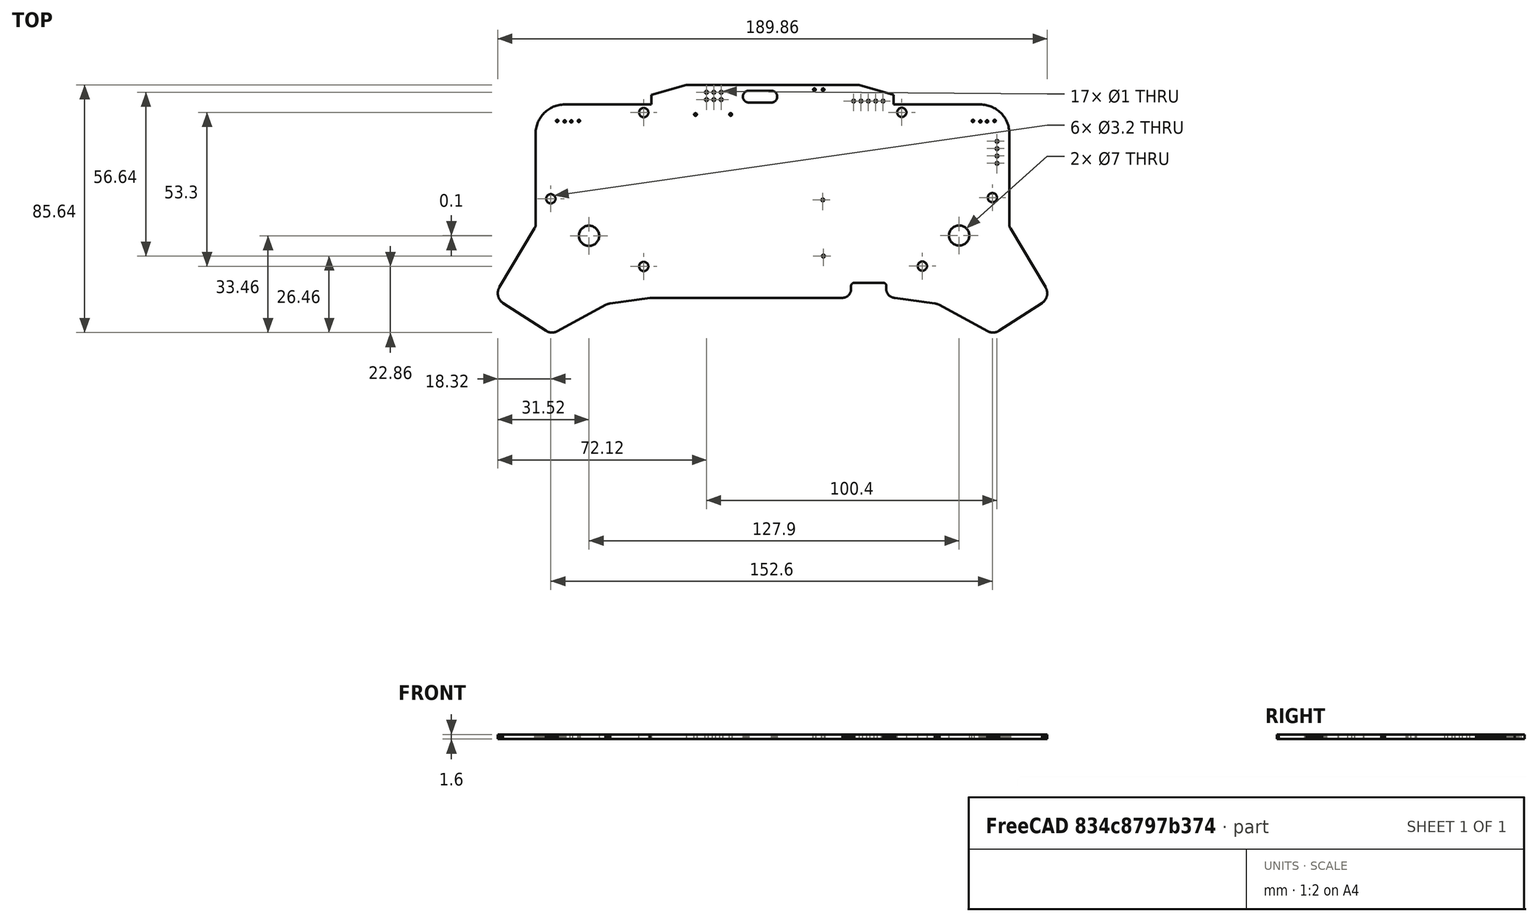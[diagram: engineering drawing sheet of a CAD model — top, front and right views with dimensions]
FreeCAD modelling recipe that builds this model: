
FCSTD DOCUMENT  (FreeCAD 0.21R33771 (Git))
Label: MilkFront
License: All rights reserved
LicenseURL: http://en.wikipedia.org/wiki/All_rights_reserved
objects: App::Part×4, Sketcher::SketchObject×2, PartDesign::CoordinateSystem×1, Part::Feature×1, PartDesign::ShapeBinder×1, PartDesign::Body×1
note: 6 computed .brp shape members not serialized (recipe doc carries the construction recipe); baked Part::Feature solids carry a one-line shape summary decoded from their .brp

FEATURE [PartDesign::CoordinateSystem] Local_CS_514c
  AttacherType = Attacher::AttachEngine3D
  MapMode = 2
  Support = -> [X_Axis003]
FEATURE [Part::Feature] Pcb_514c
  shape: bbox 189.9 x 85.64 x 1.6 mm, 543 faces (baked)
FEATURE [Sketcher::SketchObject] PCB_Sketch_514c
  FullyConstrained = false
  sketch-geometry (504):
    g0: LineSegment StartX=150.224 StartY=-25.4 StartZ=0 EndX=158 EndY=-25.4 EndZ=0
    g1: LineSegment StartX=158 StartY=-25.4 StartZ=0 EndX=158.106 EndY=-25.403 EndZ=0
    g2: LineSegment StartX=158.106 StartY=-25.403 StartZ=0 EndX=158.21 EndY=-25.4113 EndZ=0
    g3: LineSegment StartX=158.21 StartY=-25.4113 StartZ=0 EndX=158.312 EndY=-25.4246 EndZ=0
    g4: LineSegment StartX=158.312 StartY=-25.4246 StartZ=0 EndX=158.413 EndY=-25.443 EndZ=0
    g5: LineSegment StartX=158.413 StartY=-25.443 StartZ=0 EndX=158.513 EndY=-25.4662 EndZ=0
    g6: LineSegment StartX=158.513 StartY=-25.4662 StartZ=0 EndX=158.61 EndY=-25.4941 EndZ=0
    g7: LineSegment StartX=158.61 StartY=-25.4941 StartZ=0 EndX=158.705 EndY=-25.5266 EndZ=0
    g8: LineSegment StartX=158.705 StartY=-25.5266 StartZ=0 EndX=158.798 EndY=-25.5636 EndZ=0
    g9: LineSegment StartX=158.798 StartY=-25.5636 StartZ=0 EndX=158.889 EndY=-25.6049 EndZ=0
    g10: LineSegment StartX=158.889 StartY=-25.6049 StartZ=0 EndX=158.978 EndY=-25.6505 EndZ=0
    g11: LineSegment StartX=158.978 StartY=-25.6505 StartZ=0 EndX=159.063 EndY=-25.7001 EndZ=0
    g12: LineSegment StartX=159.063 StartY=-25.7001 StartZ=0 EndX=159.147 EndY=-25.7536 EndZ=0
    g13: LineSegment StartX=159.147 StartY=-25.7536 StartZ=0 EndX=159.227 EndY=-25.811 EndZ=0
    g14: LineSegment StartX=159.227 StartY=-25.811 StartZ=0 EndX=159.304 EndY=-25.8721 EndZ=0
    g15: LineSegment StartX=159.304 StartY=-25.8721 StartZ=0 EndX=159.379 EndY=-25.9367 EndZ=0
    g16: LineSegment StartX=159.379 StartY=-25.9367 StartZ=0 EndX=159.45 EndY=-26.0048 EndZ=0
    g17: LineSegment StartX=159.45 StartY=-26.0048 StartZ=0 EndX=159.518 EndY=-26.0762 EndZ=0
    g18: LineSegment StartX=159.518 StartY=-26.0762 StartZ=0 EndX=159.582 EndY=-26.1508 EndZ=0
    g19: LineSegment StartX=159.582 StartY=-26.1508 StartZ=0 EndX=159.643 EndY=-26.2284 EndZ=0
    g20: LineSegment StartX=159.643 StartY=-26.2284 StartZ=0 EndX=159.7 EndY=-26.3089 EndZ=0
    g21: LineSegment StartX=159.7 StartY=-26.3089 StartZ=0 EndX=159.753 EndY=-26.3923 EndZ=0
    g22: LineSegment StartX=159.753 StartY=-26.3923 StartZ=0 EndX=159.803 EndY=-26.4783 EndZ=0
    g23: LineSegment StartX=159.803 StartY=-26.4783 StartZ=0 EndX=159.848 EndY=-26.5668 EndZ=0
    g24: LineSegment StartX=159.848 StartY=-26.5668 StartZ=0 EndX=159.889 EndY=-26.6578 EndZ=0
    g25: LineSegment StartX=159.889 StartY=-26.6578 StartZ=0 EndX=159.926 EndY=-26.751 EndZ=0
    g26: LineSegment StartX=159.926 StartY=-26.751 StartZ=0 EndX=159.958 EndY=-26.8464 EndZ=0
    g27: LineSegment StartX=159.958 StartY=-26.8464 StartZ=0 EndX=159.985 EndY=-26.9438 EndZ=0
    g28: LineSegment StartX=159.985 StartY=-26.9438 StartZ=0 EndX=160.008 EndY=-27.0431 EndZ=0
    g29: LineSegment StartX=160.008 StartY=-27.0431 StartZ=0 EndX=160.026 EndY=-27.1442 EndZ=0
    g30: LineSegment StartX=160.026 StartY=-27.1442 StartZ=0 EndX=160.039 EndY=-27.2469 EndZ=0
    g31: LineSegment StartX=160.039 StartY=-27.2469 StartZ=0 EndX=160.047 EndY=-27.3511 EndZ=0
    g32: LineSegment StartX=160.047 StartY=-27.3511 StartZ=0 EndX=160.05 EndY=-27.4567 EndZ=0
    g33: LineSegment StartX=160.05 StartY=-27.4567 StartZ=0 EndX=160.047 EndY=-27.5623 EndZ=0
    g34: LineSegment StartX=160.047 StartY=-27.5623 StartZ=0 EndX=160.039 EndY=-27.6665 EndZ=0
    g35: LineSegment StartX=160.039 StartY=-27.6665 StartZ=0 EndX=160.026 EndY=-27.7692 EndZ=0
    g36: LineSegment StartX=160.026 StartY=-27.7692 StartZ=0 EndX=160.008 EndY=-27.8702 EndZ=0
    g37: LineSegment StartX=160.008 StartY=-27.8702 StartZ=0 EndX=159.985 EndY=-27.9695 EndZ=0
    g38: LineSegment StartX=159.985 StartY=-27.9695 StartZ=0 EndX=159.958 EndY=-28.0669 EndZ=0
    g39: LineSegment StartX=159.958 StartY=-28.0669 StartZ=0 EndX=159.926 EndY=-28.1623 EndZ=0
    g40: LineSegment StartX=159.926 StartY=-28.1623 StartZ=0 EndX=159.889 EndY=-28.2555 EndZ=0
    g41: LineSegment StartX=159.889 StartY=-28.2555 StartZ=0 EndX=159.848 EndY=-28.3465 EndZ=0
    g42: LineSegment StartX=159.848 StartY=-28.3465 StartZ=0 EndX=159.803 EndY=-28.435 EndZ=0
    g43: LineSegment StartX=159.803 StartY=-28.435 StartZ=0 EndX=159.753 EndY=-28.521 EndZ=0
    g44: LineSegment StartX=159.753 StartY=-28.521 StartZ=0 EndX=159.7 EndY=-28.6044 EndZ=0
    g45: LineSegment StartX=159.7 StartY=-28.6044 StartZ=0 EndX=159.643 EndY=-28.6849 EndZ=0
    g46: LineSegment StartX=159.643 StartY=-28.6849 StartZ=0 EndX=159.582 EndY=-28.7625 EndZ=0
    g47: LineSegment StartX=159.582 StartY=-28.7625 StartZ=0 EndX=159.518 EndY=-28.8371 EndZ=0
    g48: LineSegment StartX=159.518 StartY=-28.8371 StartZ=0 EndX=159.45 EndY=-28.9085 EndZ=0
    g49: LineSegment StartX=159.45 StartY=-28.9085 StartZ=0 EndX=159.379 EndY=-28.9766 EndZ=0
    g50: LineSegment StartX=159.379 StartY=-28.9766 StartZ=0 EndX=159.304 EndY=-29.0412 EndZ=0
    g51: LineSegment StartX=159.304 StartY=-29.0412 StartZ=0 EndX=159.227 EndY=-29.1023 EndZ=0
    g52: LineSegment StartX=159.227 StartY=-29.1023 StartZ=0 EndX=159.147 EndY=-29.1597 EndZ=0
    g53: LineSegment StartX=159.147 StartY=-29.1597 StartZ=0 EndX=159.063 EndY=-29.2133 EndZ=0
    g54: LineSegment StartX=159.063 StartY=-29.2133 StartZ=0 EndX=158.978 EndY=-29.2629 EndZ=0
    g55: LineSegment StartX=158.978 StartY=-29.2629 StartZ=0 EndX=158.889 EndY=-29.3084 EndZ=0
    g56: LineSegment StartX=158.889 StartY=-29.3084 StartZ=0 EndX=158.798 EndY=-29.3497 EndZ=0
    g57: LineSegment StartX=158.798 StartY=-29.3497 StartZ=0 EndX=158.705 EndY=-29.3867 EndZ=0
    g58: LineSegment StartX=158.705 StartY=-29.3867 StartZ=0 EndX=158.61 EndY=-29.4192 EndZ=0
    g59: LineSegment StartX=158.61 StartY=-29.4192 StartZ=0 EndX=158.513 EndY=-29.4471 EndZ=0
    g60: LineSegment StartX=158.513 StartY=-29.4471 StartZ=0 EndX=158.413 EndY=-29.4703 EndZ=0
    g61: LineSegment StartX=158.413 StartY=-29.4703 StartZ=0 EndX=158.312 EndY=-29.4887 EndZ=0
    g62: LineSegment StartX=158.312 StartY=-29.4887 StartZ=0 EndX=158.21 EndY=-29.5021 EndZ=0
    g63: LineSegment StartX=158.21 StartY=-29.5021 StartZ=0 EndX=158.106 EndY=-29.5103 EndZ=0
    g64: LineSegment StartX=158.106 StartY=-29.5103 StartZ=0 EndX=158 EndY=-29.5133 EndZ=0
    g65: LineSegment StartX=158 StartY=-29.5133 StartZ=0 EndX=150.224 EndY=-29.5133 EndZ=0
    g66: LineSegment StartX=150.224 StartY=-29.5133 StartZ=0 EndX=150.119 EndY=-29.5102 EndZ=0
    g67: LineSegment StartX=150.119 StartY=-29.5102 StartZ=0 EndX=150.014 EndY=-29.5019 EndZ=0
    g68: LineSegment StartX=150.014 StartY=-29.5019 StartZ=0 EndX=149.912 EndY=-29.4884 EndZ=0
    g69: LineSegment StartX=149.912 StartY=-29.4884 StartZ=0 EndX=149.811 EndY=-29.47 EndZ=0
    g70: LineSegment StartX=149.811 StartY=-29.47 StartZ=0 EndX=149.712 EndY=-29.4468 EndZ=0
    g71: LineSegment StartX=149.712 StartY=-29.4468 StartZ=0 EndX=149.614 EndY=-29.4188 EndZ=0
    g72: LineSegment StartX=149.614 StartY=-29.4188 StartZ=0 EndX=149.519 EndY=-29.3863 EndZ=0
    g73: LineSegment StartX=149.519 StartY=-29.3863 StartZ=0 EndX=149.426 EndY=-29.3493 EndZ=0
    g74: LineSegment StartX=149.426 StartY=-29.3493 StartZ=0 EndX=149.335 EndY=-29.3079 EndZ=0
    g75: LineSegment StartX=149.335 StartY=-29.3079 StartZ=0 EndX=149.247 EndY=-29.2623 EndZ=0
    g76: LineSegment StartX=149.247 StartY=-29.2623 StartZ=0 EndX=149.161 EndY=-29.2127 EndZ=0
    g77: LineSegment StartX=149.161 StartY=-29.2127 StartZ=0 EndX=149.078 EndY=-29.1591 EndZ=0
    g78: LineSegment StartX=149.078 StartY=-29.1591 StartZ=0 EndX=148.998 EndY=-29.1017 EndZ=0
    g79: LineSegment StartX=148.998 StartY=-29.1017 StartZ=0 EndX=148.921 EndY=-29.0407 EndZ=0
    g80: LineSegment StartX=148.921 StartY=-29.0407 StartZ=0 EndX=148.846 EndY=-28.976 EndZ=0
    g81: LineSegment StartX=148.846 StartY=-28.976 StartZ=0 EndX=148.775 EndY=-28.9079 EndZ=0
    g82: LineSegment StartX=148.775 StartY=-28.9079 StartZ=0 EndX=148.707 EndY=-28.8366 EndZ=0
    g83: LineSegment StartX=148.707 StartY=-28.8366 StartZ=0 EndX=148.643 EndY=-28.762 EndZ=0
    g84: LineSegment StartX=148.643 StartY=-28.762 StartZ=0 EndX=148.582 EndY=-28.6844 EndZ=0
    g85: LineSegment StartX=148.582 StartY=-28.6844 StartZ=0 EndX=148.525 EndY=-28.6039 EndZ=0
    g86: LineSegment StartX=148.525 StartY=-28.6039 StartZ=0 EndX=148.472 EndY=-28.5205 EndZ=0
    g87: LineSegment StartX=148.472 StartY=-28.5205 StartZ=0 EndX=148.423 EndY=-28.4346 EndZ=0
    g88: LineSegment StartX=148.423 StartY=-28.4346 StartZ=0 EndX=148.378 EndY=-28.3461 EndZ=0
    g89: LineSegment StartX=148.378 StartY=-28.3461 StartZ=0 EndX=148.337 EndY=-28.2551 EndZ=0
    g90: LineSegment StartX=148.337 StartY=-28.2551 StartZ=0 EndX=148.3 EndY=-28.1619 EndZ=0
    g91: LineSegment StartX=148.3 StartY=-28.1619 StartZ=0 EndX=148.268 EndY=-28.0666 EndZ=0
    g92: LineSegment StartX=148.268 StartY=-28.0666 StartZ=0 EndX=148.24 EndY=-27.9692 EndZ=0
    g93: LineSegment StartX=148.24 StartY=-27.9692 StartZ=0 EndX=148.217 EndY=-27.87 EndZ=0
    g94: LineSegment StartX=148.217 StartY=-27.87 StartZ=0 EndX=148.199 EndY=-27.769 EndZ=0
    g95: LineSegment StartX=148.199 StartY=-27.769 StartZ=0 EndX=148.186 EndY=-27.6663 EndZ=0
    g96: LineSegment StartX=148.186 StartY=-27.6663 StartZ=0 EndX=148.179 EndY=-27.5622 EndZ=0
    g97: LineSegment StartX=148.179 StartY=-27.5622 StartZ=0 EndX=148.176 EndY=-27.4566 EndZ=0
    g98: LineSegment StartX=148.176 StartY=-27.4566 StartZ=0 EndX=148.179 EndY=-27.3511 EndZ=0
    g99: LineSegment StartX=148.179 StartY=-27.3511 StartZ=0 EndX=148.186 EndY=-27.247 EndZ=0
    g100: LineSegment StartX=148.186 StartY=-27.247 StartZ=0 EndX=148.199 EndY=-27.1443 EndZ=0
    g101: LineSegment StartX=148.199 StartY=-27.1443 StartZ=0 EndX=148.217 EndY=-27.0433 EndZ=0
    g102: LineSegment StartX=148.217 StartY=-27.0433 StartZ=0 EndX=148.24 EndY=-26.944 EndZ=0
    g103: LineSegment StartX=148.24 StartY=-26.944 StartZ=0 EndX=148.268 EndY=-26.8467 EndZ=0
    g104: LineSegment StartX=148.268 StartY=-26.8467 StartZ=0 EndX=148.3 EndY=-26.7513 EndZ=0
    g105: LineSegment StartX=148.3 StartY=-26.7513 StartZ=0 EndX=148.337 EndY=-26.6581 EndZ=0
    g106: LineSegment StartX=148.337 StartY=-26.6581 StartZ=0 EndX=148.378 EndY=-26.5672 EndZ=0
    g107: LineSegment StartX=148.378 StartY=-26.5672 StartZ=0 EndX=148.423 EndY=-26.4787 EndZ=0
    g108: LineSegment StartX=148.423 StartY=-26.4787 StartZ=0 EndX=148.472 EndY=-26.3927 EndZ=0
    g109: LineSegment StartX=148.472 StartY=-26.3927 StartZ=0 EndX=148.525 EndY=-26.3094 EndZ=0
    g110: LineSegment StartX=148.525 StartY=-26.3094 StartZ=0 EndX=148.582 EndY=-26.2289 EndZ=0
    g111: LineSegment StartX=148.582 StartY=-26.2289 StartZ=0 EndX=148.643 EndY=-26.1513 EndZ=0
    g112: LineSegment StartX=148.643 StartY=-26.1513 StartZ=0 EndX=148.707 EndY=-26.0767 EndZ=0
    g113: LineSegment StartX=148.707 StartY=-26.0767 StartZ=0 EndX=148.775 EndY=-26.0053 EndZ=0
    g114: LineSegment StartX=148.775 StartY=-26.0053 StartZ=0 EndX=148.846 EndY=-25.9373 EndZ=0
    g115: LineSegment StartX=148.846 StartY=-25.9373 StartZ=0 EndX=148.921 EndY=-25.8726 EndZ=0
    g116: LineSegment StartX=148.921 StartY=-25.8726 StartZ=0 EndX=148.998 EndY=-25.8115 EndZ=0
    g117: LineSegment StartX=148.998 StartY=-25.8115 StartZ=0 EndX=149.078 EndY=-25.7541 EndZ=0
    g118: LineSegment StartX=149.078 StartY=-25.7541 StartZ=0 EndX=149.161 EndY=-25.7006 EndZ=0
    g119: LineSegment StartX=149.161 StartY=-25.7006 StartZ=0 EndX=149.247 EndY=-25.6509 EndZ=0
    g120: LineSegment StartX=149.247 StartY=-25.6509 StartZ=0 EndX=149.335 EndY=-25.6054 EndZ=0
    g121: LineSegment StartX=149.335 StartY=-25.6054 StartZ=0 EndX=149.426 EndY=-25.564 EndZ=0
    g122: LineSegment StartX=149.426 StartY=-25.564 StartZ=0 EndX=149.519 EndY=-25.527 EndZ=0
    g123: LineSegment StartX=149.519 StartY=-25.527 StartZ=0 EndX=149.614 EndY=-25.4945 EndZ=0
    g124: LineSegment StartX=149.614 StartY=-25.4945 StartZ=0 EndX=149.712 EndY=-25.4665 EndZ=0
    g125: LineSegment StartX=149.712 StartY=-25.4665 StartZ=0 EndX=149.811 EndY=-25.4432 EndZ=0
    g126: LineSegment StartX=149.811 StartY=-25.4432 StartZ=0 EndX=149.912 EndY=-25.4248 EndZ=0
    g127: LineSegment StartX=149.912 StartY=-25.4248 StartZ=0 EndX=150.014 EndY=-25.4114 EndZ=0
    g128: LineSegment StartX=150.014 StartY=-25.4114 StartZ=0 EndX=150.119 EndY=-25.4031 EndZ=0
    g129: LineSegment StartX=150.119 StartY=-25.4031 StartZ=0 EndX=150.224 EndY=-25.4 EndZ=0
    g130: LineSegment StartX=188.25 StartY=-23.4173 StartZ=0 EndX=200.25 EndY=-26.9154 EndZ=0
    g131: LineSegment StartX=200.25 StartY=-26.9154 StartZ=0 EndX=200.25 EndY=-30.1929 EndZ=0
    g132: LineSegment StartX=200.25 StartY=-30.1929 StartZ=0 EndX=230.25 EndY=-30.1929 EndZ=0
    g133: LineSegment StartX=230.25 StartY=-30.1929 StartZ=0 EndX=230.746 EndY=-30.2052 EndZ=0
    g134: LineSegment StartX=230.746 StartY=-30.2052 StartZ=0 EndX=231.238 EndY=-30.2418 EndZ=0
    g135: LineSegment StartX=231.238 StartY=-30.2418 StartZ=0 EndX=231.726 EndY=-30.3025 EndZ=0
    g136: LineSegment StartX=231.726 StartY=-30.3025 StartZ=0 EndX=232.21 EndY=-30.3868 EndZ=0
    g137: LineSegment StartX=232.21 StartY=-30.3868 StartZ=0 EndX=232.687 EndY=-30.4945 EndZ=0
    g138: LineSegment StartX=232.687 StartY=-30.4945 StartZ=0 EndX=233.158 EndY=-30.6251 EndZ=0
    g139: LineSegment StartX=233.158 StartY=-30.6251 StartZ=0 EndX=233.621 EndY=-30.7784 EndZ=0
    g140: LineSegment StartX=233.621 StartY=-30.7784 StartZ=0 EndX=234.077 EndY=-30.9541 EndZ=0
    g141: LineSegment StartX=234.077 StartY=-30.9541 StartZ=0 EndX=234.523 EndY=-31.1517 EndZ=0
    g142: LineSegment StartX=234.523 StartY=-31.1517 StartZ=0 EndX=234.959 EndY=-31.3709 EndZ=0
    g143: LineSegment StartX=234.959 StartY=-31.3709 StartZ=0 EndX=235.384 EndY=-31.6115 EndZ=0
    g144: LineSegment StartX=235.384 StartY=-31.6115 StartZ=0 EndX=235.798 EndY=-31.873 EndZ=0
    g145: LineSegment StartX=235.798 StartY=-31.873 StartZ=0 EndX=236.199 EndY=-32.1551 EndZ=0
    g146: LineSegment StartX=236.199 StartY=-32.1551 StartZ=0 EndX=236.587 EndY=-32.4575 EndZ=0
    g147: LineSegment StartX=236.587 StartY=-32.4575 StartZ=0 EndX=236.961 EndY=-32.7799 EndZ=0
    g148: LineSegment StartX=236.961 StartY=-32.7799 StartZ=0 EndX=237.321 EndY=-33.1218 EndZ=0
    g149: LineSegment StartX=237.321 StartY=-33.1218 StartZ=0 EndX=237.663 EndY=-33.4811 EndZ=0
    g150: LineSegment StartX=237.663 StartY=-33.4811 StartZ=0 EndX=237.985 EndY=-33.8553 EndZ=0
    g151: LineSegment StartX=237.985 StartY=-33.8553 StartZ=0 EndX=238.287 EndY=-34.2435 EndZ=0
    g152: LineSegment StartX=238.287 StartY=-34.2435 StartZ=0 EndX=238.57 EndY=-34.6449 EndZ=0
    g153: LineSegment StartX=238.57 StartY=-34.6449 StartZ=0 EndX=238.831 EndY=-35.0587 EndZ=0
    g154: LineSegment StartX=238.831 StartY=-35.0587 StartZ=0 EndX=239.072 EndY=-35.484 EndZ=0
    g155: LineSegment StartX=239.072 StartY=-35.484 StartZ=0 EndX=239.291 EndY=-35.9201 EndZ=0
    g156: LineSegment StartX=239.291 StartY=-35.9201 StartZ=0 EndX=239.488 EndY=-36.3661 EndZ=0
    g157: LineSegment StartX=239.488 StartY=-36.3661 StartZ=0 EndX=239.664 EndY=-36.8212 EndZ=0
    g158: LineSegment StartX=239.664 StartY=-36.8212 StartZ=0 EndX=239.817 EndY=-37.2845 EndZ=0
    g159: LineSegment StartX=239.817 StartY=-37.2845 StartZ=0 EndX=239.948 EndY=-37.7554 EndZ=0
    g160: LineSegment StartX=239.948 StartY=-37.7554 StartZ=0 EndX=240.056 EndY=-38.2329 EndZ=0
    g161: LineSegment StartX=240.056 StartY=-38.2329 StartZ=0 EndX=240.14 EndY=-38.7162 EndZ=0
    g162: LineSegment StartX=240.14 StartY=-38.7162 StartZ=0 EndX=240.201 EndY=-39.2045 EndZ=0
    g163: LineSegment StartX=240.201 StartY=-39.2045 StartZ=0 EndX=240.237 EndY=-39.697 EndZ=0
    g164: LineSegment StartX=240.237 StartY=-39.697 StartZ=0 EndX=240.25 EndY=-40.1929 EndZ=0
    g165: LineSegment StartX=240.25 StartY=-40.1929 StartZ=0 EndX=240.25 EndY=-71.7127 EndZ=0
    g166: LineSegment StartX=240.25 StartY=-71.7127 StartZ=0 EndX=240.251 EndY=-71.7971 EndZ=0
    g167: LineSegment StartX=240.251 StartY=-71.7971 StartZ=0 EndX=240.255 EndY=-71.8813 EndZ=0
    g168: LineSegment StartX=240.255 StartY=-71.8813 StartZ=0 EndX=240.262 EndY=-71.9651 EndZ=0
    g169: LineSegment StartX=240.262 StartY=-71.9651 StartZ=0 EndX=240.272 EndY=-72.0485 EndZ=0
    g170: LineSegment StartX=240.272 StartY=-72.0485 StartZ=0 EndX=240.285 EndY=-72.1315 EndZ=0
    g171: LineSegment StartX=240.285 StartY=-72.1315 StartZ=0 EndX=240.3 EndY=-72.2139 EndZ=0
    g172: LineSegment StartX=240.3 StartY=-72.2139 StartZ=0 EndX=240.319 EndY=-72.2957 EndZ=0
    g173: LineSegment StartX=240.319 StartY=-72.2957 StartZ=0 EndX=240.339 EndY=-72.3769 EndZ=0
    g174: LineSegment StartX=240.339 StartY=-72.3769 StartZ=0 EndX=240.363 EndY=-72.4573 EndZ=0
    g175: LineSegment StartX=240.363 StartY=-72.4573 StartZ=0 EndX=240.389 EndY=-72.5368 EndZ=0
    g176: LineSegment StartX=240.389 StartY=-72.5368 StartZ=0 EndX=240.418 EndY=-72.6155 EndZ=0
    g177: LineSegment StartX=240.418 StartY=-72.6155 StartZ=0 EndX=240.45 EndY=-72.6933 EndZ=0
    g178: LineSegment StartX=240.45 StartY=-72.6933 StartZ=0 EndX=240.484 EndY=-72.77 EndZ=0
    g179: LineSegment StartX=240.484 StartY=-72.77 StartZ=0 EndX=240.521 EndY=-72.8456 EndZ=0
    g180: LineSegment StartX=240.521 StartY=-72.8456 StartZ=0 EndX=240.561 EndY=-72.9201 EndZ=0
    g181: LineSegment StartX=240.561 StartY=-72.9201 StartZ=0 EndX=240.603 EndY=-72.9933 EndZ=0
    g182: LineSegment StartX=240.603 StartY=-72.9933 StartZ=0 EndX=252.778 EndY=-93.4073 EndZ=0
    g183: LineSegment StartX=252.778 StartY=-93.4073 StartZ=0 EndX=252.877 EndY=-93.5819 EndZ=0
    g184: LineSegment StartX=252.877 StartY=-93.5819 StartZ=0 EndX=252.965 EndY=-93.7593 EndZ=0
    g185: LineSegment StartX=252.965 StartY=-93.7593 StartZ=0 EndX=253.045 EndY=-93.9392 EndZ=0
    g186: LineSegment StartX=253.045 StartY=-93.9392 StartZ=0 EndX=253.114 EndY=-94.1214 EndZ=0
    g187: LineSegment StartX=253.114 StartY=-94.1214 StartZ=0 EndX=253.175 EndY=-94.3054 EndZ=0
    g188: LineSegment StartX=253.175 StartY=-94.3054 StartZ=0 EndX=253.226 EndY=-94.491 EndZ=0
    g189: LineSegment StartX=253.226 StartY=-94.491 StartZ=0 EndX=253.267 EndY=-94.6778 EndZ=0
    g190: LineSegment StartX=253.267 StartY=-94.6778 StartZ=0 EndX=253.3 EndY=-94.8655 EndZ=0
    g191: LineSegment StartX=253.3 StartY=-94.8655 StartZ=0 EndX=253.323 EndY=-95.0538 EndZ=0
    g192: LineSegment StartX=253.323 StartY=-95.0538 StartZ=0 EndX=253.338 EndY=-95.2424 EndZ=0
    g193: LineSegment StartX=253.338 StartY=-95.2424 StartZ=0 EndX=253.343 EndY=-95.4309 EndZ=0
    g194: LineSegment StartX=253.343 StartY=-95.4309 StartZ=0 EndX=253.34 EndY=-95.6191 EndZ=0
    g195: LineSegment StartX=253.34 StartY=-95.6191 StartZ=0 EndX=253.328 EndY=-95.8066 EndZ=0
    g196: LineSegment StartX=253.328 StartY=-95.8066 StartZ=0 EndX=253.307 EndY=-95.993 EndZ=0
    g197: LineSegment StartX=253.307 StartY=-95.993 StartZ=0 EndX=253.277 EndY=-96.1782 EndZ=0
    g198: LineSegment StartX=253.277 StartY=-96.1782 StartZ=0 EndX=253.239 EndY=-96.3617 EndZ=0
    g199: LineSegment StartX=253.239 StartY=-96.3617 StartZ=0 EndX=253.192 EndY=-96.5432 EndZ=0
    g200: LineSegment StartX=253.192 StartY=-96.5432 StartZ=0 EndX=253.137 EndY=-96.7224 EndZ=0
    g201: LineSegment StartX=253.137 StartY=-96.7224 StartZ=0 EndX=253.074 EndY=-96.8989 EndZ=0
    g202: LineSegment StartX=253.074 StartY=-96.8989 StartZ=0 EndX=253.002 EndY=-97.0726 EndZ=0
    g203: LineSegment StartX=253.002 StartY=-97.0726 StartZ=0 EndX=252.922 EndY=-97.243 EndZ=0
    g204: LineSegment StartX=252.922 StartY=-97.243 StartZ=0 EndX=252.834 EndY=-97.4098 EndZ=0
    g205: LineSegment StartX=252.834 StartY=-97.4098 StartZ=0 EndX=252.738 EndY=-97.5727 EndZ=0
    g206: LineSegment StartX=252.738 StartY=-97.5727 StartZ=0 EndX=252.634 EndY=-97.7314 EndZ=0
    g207: LineSegment StartX=252.634 StartY=-97.7314 StartZ=0 EndX=252.522 EndY=-97.8855 EndZ=0
    g208: LineSegment StartX=252.522 StartY=-97.8855 StartZ=0 EndX=252.402 EndY=-98.0347 EndZ=0
    g209: LineSegment StartX=252.402 StartY=-98.0347 StartZ=0 EndX=252.275 EndY=-98.1788 EndZ=0
    g210: LineSegment StartX=252.275 StartY=-98.1788 StartZ=0 EndX=252.139 EndY=-98.3174 EndZ=0
    g211: LineSegment StartX=252.139 StartY=-98.3174 StartZ=0 EndX=251.996 EndY=-98.4501 EndZ=0
    g212: LineSegment StartX=251.996 StartY=-98.4501 StartZ=0 EndX=251.846 EndY=-98.5767 EndZ=0
    g213: LineSegment StartX=251.846 StartY=-98.5767 StartZ=0 EndX=251.688 EndY=-98.6968 EndZ=0
    g214: LineSegment StartX=251.688 StartY=-98.6968 StartZ=0 EndX=251.523 EndY=-98.8101 EndZ=0
    g215: LineSegment StartX=251.523 StartY=-98.8101 StartZ=0 EndX=236.753 EndY=-108.411 EndZ=0
    g216: LineSegment StartX=236.753 StartY=-108.411 StartZ=0 EndX=236.517 EndY=-108.552 EndZ=0
    g217: LineSegment StartX=236.517 StartY=-108.552 StartZ=0 EndX=236.275 EndY=-108.677 EndZ=0
    g218: LineSegment StartX=236.275 StartY=-108.677 StartZ=0 EndX=236.027 EndY=-108.783 EndZ=0
    g219: LineSegment StartX=236.027 StartY=-108.783 StartZ=0 EndX=235.773 EndY=-108.873 EndZ=0
    g220: LineSegment StartX=235.773 StartY=-108.873 StartZ=0 EndX=235.515 EndY=-108.944 EndZ=0
    g221: LineSegment StartX=235.515 StartY=-108.944 StartZ=0 EndX=235.254 EndY=-108.999 EndZ=0
    g222: LineSegment StartX=235.254 StartY=-108.999 StartZ=0 EndX=234.99 EndY=-109.035 EndZ=0
    g223: LineSegment StartX=234.99 StartY=-109.035 StartZ=0 EndX=234.725 EndY=-109.054 EndZ=0
    g224: LineSegment StartX=234.725 StartY=-109.054 StartZ=0 EndX=234.459 EndY=-109.055 EndZ=0
    g225: LineSegment StartX=234.459 StartY=-109.055 StartZ=0 EndX=234.193 EndY=-109.039 EndZ=0
    g226: LineSegment StartX=234.193 StartY=-109.039 StartZ=0 EndX=233.928 EndY=-109.005 EndZ=0
    g227: LineSegment StartX=233.928 StartY=-109.005 StartZ=0 EndX=233.665 EndY=-108.953 EndZ=0
    g228: LineSegment StartX=233.665 StartY=-108.953 StartZ=0 EndX=233.406 EndY=-108.883 EndZ=0
    g229: LineSegment StartX=233.406 StartY=-108.883 StartZ=0 EndX=233.15 EndY=-108.795 EndZ=0
    g230: LineSegment StartX=233.15 StartY=-108.795 StartZ=0 EndX=232.899 EndY=-108.69 EndZ=0
    g231: LineSegment StartX=232.899 StartY=-108.69 StartZ=0 EndX=232.654 EndY=-108.567 EndZ=0
    g232: LineSegment StartX=232.654 StartY=-108.567 StartZ=0 EndX=216.148 EndY=-99.5417 EndZ=0
    g233: LineSegment StartX=216.148 StartY=-99.5417 StartZ=0 EndX=216.049 EndY=-99.4887 EndZ=0
    g234: LineSegment StartX=216.049 StartY=-99.4887 StartZ=0 EndX=215.948 EndY=-99.438 EndZ=0
    g235: LineSegment StartX=215.948 StartY=-99.438 StartZ=0 EndX=215.847 EndY=-99.3897 EndZ=0
    g236: LineSegment StartX=215.847 StartY=-99.3897 StartZ=0 EndX=215.744 EndY=-99.3436 EndZ=0
    g237: LineSegment StartX=215.744 StartY=-99.3436 StartZ=0 EndX=215.64 EndY=-99.2999 EndZ=0
    g238: LineSegment StartX=215.64 StartY=-99.2999 StartZ=0 EndX=215.536 EndY=-99.2586 EndZ=0
    g239: LineSegment StartX=215.536 StartY=-99.2586 StartZ=0 EndX=215.43 EndY=-99.2196 EndZ=0
    g240: LineSegment StartX=215.43 StartY=-99.2196 StartZ=0 EndX=215.324 EndY=-99.183 EndZ=0
    g241: LineSegment StartX=215.324 StartY=-99.183 StartZ=0 EndX=215.217 EndY=-99.1488 EndZ=0
    g242: LineSegment StartX=215.217 StartY=-99.1488 StartZ=0 EndX=215.109 EndY=-99.117 EndZ=0
    g243: LineSegment StartX=215.109 StartY=-99.117 StartZ=0 EndX=215 EndY=-99.0877 EndZ=0
    g244: LineSegment StartX=215 StartY=-99.0877 StartZ=0 EndX=214.891 EndY=-99.0608 EndZ=0
    g245: LineSegment StartX=214.891 StartY=-99.0608 StartZ=0 EndX=214.781 EndY=-99.0363 EndZ=0
    g246: LineSegment StartX=214.781 StartY=-99.0363 StartZ=0 EndX=214.671 EndY=-99.0143 EndZ=0
    g247: LineSegment StartX=214.671 StartY=-99.0143 StartZ=0 EndX=214.56 EndY=-98.9948 EndZ=0
    g248: LineSegment StartX=214.56 StartY=-98.9948 StartZ=0 EndX=214.448 EndY=-98.9778 EndZ=0
    g249: LineSegment StartX=214.448 StartY=-98.9778 StartZ=0 EndX=200.75 EndY=-97.0446 EndZ=0
    g250: LineSegment StartX=200.75 StartY=-97.0446 StartZ=0 EndX=200.731 EndY=-97.0446 EndZ=0
    g251: LineSegment StartX=200.731 StartY=-97.0446 StartZ=0 EndX=200.583 EndY=-97.0409 EndZ=0
    g252: LineSegment StartX=200.583 StartY=-97.0409 StartZ=0 EndX=200.435 EndY=-97.0299 EndZ=0
    g253: LineSegment StartX=200.435 StartY=-97.0299 StartZ=0 EndX=200.288 EndY=-97.0118 EndZ=0
    g254: LineSegment StartX=200.288 StartY=-97.0118 StartZ=0 EndX=200.143 EndY=-96.9865 EndZ=0
    g255: LineSegment StartX=200.143 StartY=-96.9865 StartZ=0 EndX=200 EndY=-96.9542 EndZ=0
    g256: LineSegment StartX=200 StartY=-96.9542 StartZ=0 EndX=199.859 EndY=-96.915 EndZ=0
    g257: LineSegment StartX=199.859 StartY=-96.915 StartZ=0 EndX=199.72 EndY=-96.869 EndZ=0
    g258: LineSegment StartX=199.72 StartY=-96.869 StartZ=0 EndX=199.583 EndY=-96.8163 EndZ=0
    g259: LineSegment StartX=199.583 StartY=-96.8163 StartZ=0 EndX=199.449 EndY=-96.757 EndZ=0
    g260: LineSegment StartX=199.449 StartY=-96.757 StartZ=0 EndX=199.319 EndY=-96.6912 EndZ=0
    g261: LineSegment StartX=199.319 StartY=-96.6912 StartZ=0 EndX=199.191 EndY=-96.619 EndZ=0
    g262: LineSegment StartX=199.191 StartY=-96.619 StartZ=0 EndX=199.067 EndY=-96.5406 EndZ=0
    g263: LineSegment StartX=199.067 StartY=-96.5406 StartZ=0 EndX=198.946 EndY=-96.456 EndZ=0
    g264: LineSegment StartX=198.946 StartY=-96.456 StartZ=0 EndX=198.83 EndY=-96.3652 EndZ=0
    g265: LineSegment StartX=198.83 StartY=-96.3652 StartZ=0 EndX=198.718 EndY=-96.2685 EndZ=0
    g266: LineSegment StartX=198.718 StartY=-96.2685 StartZ=0 EndX=198.61 EndY=-96.1659 EndZ=0
    g267: LineSegment StartX=198.61 StartY=-96.1659 StartZ=0 EndX=198.507 EndY=-96.0581 EndZ=0
    g268: LineSegment StartX=198.507 StartY=-96.0581 StartZ=0 EndX=198.411 EndY=-95.9459 EndZ=0
    g269: LineSegment StartX=198.411 StartY=-95.9459 StartZ=0 EndX=198.32 EndY=-95.8294 EndZ=0
    g270: LineSegment StartX=198.32 StartY=-95.8294 StartZ=0 EndX=198.235 EndY=-95.709 EndZ=0
    g271: LineSegment StartX=198.235 StartY=-95.709 StartZ=0 EndX=198.157 EndY=-95.5849 EndZ=0
    g272: LineSegment StartX=198.157 StartY=-95.5849 StartZ=0 EndX=198.085 EndY=-95.4573 EndZ=0
    g273: LineSegment StartX=198.085 StartY=-95.4573 StartZ=0 EndX=198.019 EndY=-95.3265 EndZ=0
    g274: LineSegment StartX=198.019 StartY=-95.3265 StartZ=0 EndX=197.96 EndY=-95.1927 EndZ=0
    g275: LineSegment StartX=197.96 StartY=-95.1927 StartZ=0 EndX=197.907 EndY=-95.0561 EndZ=0
    g276: LineSegment StartX=197.907 StartY=-95.0561 StartZ=0 EndX=197.861 EndY=-94.9171 EndZ=0
    g277: LineSegment StartX=197.861 StartY=-94.9171 StartZ=0 EndX=197.822 EndY=-94.7759 EndZ=0
    g278: LineSegment StartX=197.822 StartY=-94.7759 StartZ=0 EndX=197.789 EndY=-94.6326 EndZ=0
    g279: LineSegment StartX=197.789 StartY=-94.6326 StartZ=0 EndX=197.764 EndY=-94.4876 EndZ=0
    g280: LineSegment StartX=197.764 StartY=-94.4876 StartZ=0 EndX=197.746 EndY=-94.3411 EndZ=0
    g281: LineSegment StartX=197.746 StartY=-94.3411 StartZ=0 EndX=197.735 EndY=-94.1934 EndZ=0
    g282: LineSegment StartX=197.735 StartY=-94.1934 StartZ=0 EndX=197.731 EndY=-94.0446 EndZ=0
    g283: LineSegment StartX=197.731 StartY=-94.0446 StartZ=0 EndX=197.731 EndY=-92.8765 EndZ=0
    g284: LineSegment StartX=197.731 StartY=-92.8765 StartZ=0 EndX=197.73 EndY=-92.8269 EndZ=0
    g285: LineSegment StartX=197.73 StartY=-92.8269 StartZ=0 EndX=197.726 EndY=-92.7777 EndZ=0
    g286: LineSegment StartX=197.726 StartY=-92.7777 StartZ=0 EndX=197.72 EndY=-92.7288 EndZ=0
    g287: LineSegment StartX=197.72 StartY=-92.7288 StartZ=0 EndX=197.712 EndY=-92.6805 EndZ=0
    g288: LineSegment StartX=197.712 StartY=-92.6805 StartZ=0 EndX=197.701 EndY=-92.6328 EndZ=0
    g289: LineSegment StartX=197.701 StartY=-92.6328 StartZ=0 EndX=197.688 EndY=-92.5857 EndZ=0
    g290: LineSegment StartX=197.688 StartY=-92.5857 StartZ=0 EndX=197.673 EndY=-92.5393 EndZ=0
    g291: LineSegment StartX=197.673 StartY=-92.5393 StartZ=0 EndX=197.655 EndY=-92.4938 EndZ=0
    g292: LineSegment StartX=197.655 StartY=-92.4938 StartZ=0 EndX=197.635 EndY=-92.4492 EndZ=0
    g293: LineSegment StartX=197.635 StartY=-92.4492 StartZ=0 EndX=197.613 EndY=-92.4056 EndZ=0
    g294: LineSegment StartX=197.613 StartY=-92.4056 StartZ=0 EndX=197.589 EndY=-92.3631 EndZ=0
    g295: LineSegment StartX=197.589 StartY=-92.3631 StartZ=0 EndX=197.563 EndY=-92.3217 EndZ=0
    g296: LineSegment StartX=197.563 StartY=-92.3217 StartZ=0 EndX=197.535 EndY=-92.2815 EndZ=0
    g297: LineSegment StartX=197.535 StartY=-92.2815 StartZ=0 EndX=197.505 EndY=-92.2427 EndZ=0
    g298: LineSegment StartX=197.505 StartY=-92.2427 StartZ=0 EndX=197.473 EndY=-92.2053 EndZ=0
    g299: LineSegment StartX=197.473 StartY=-92.2053 StartZ=0 EndX=197.438 EndY=-92.1694 EndZ=0
    g300: LineSegment StartX=197.438 StartY=-92.1694 StartZ=0 EndX=197.402 EndY=-92.1352 EndZ=0
    g301: LineSegment StartX=197.402 StartY=-92.1352 StartZ=0 EndX=197.365 EndY=-92.1029 EndZ=0
    g302: LineSegment StartX=197.365 StartY=-92.1029 StartZ=0 EndX=197.326 EndY=-92.0727 EndZ=0
    g303: LineSegment StartX=197.326 StartY=-92.0727 StartZ=0 EndX=197.286 EndY=-92.0445 EndZ=0
    g304: LineSegment StartX=197.286 StartY=-92.0445 StartZ=0 EndX=197.245 EndY=-92.0183 EndZ=0
    g305: LineSegment StartX=197.245 StartY=-92.0183 StartZ=0 EndX=197.202 EndY=-91.9943 EndZ=0
    g306: LineSegment StartX=197.202 StartY=-91.9943 StartZ=0 EndX=197.159 EndY=-91.9724 EndZ=0
    g307: LineSegment StartX=197.159 StartY=-91.9724 StartZ=0 EndX=197.114 EndY=-91.9526 EndZ=0
    g308: LineSegment StartX=197.114 StartY=-91.9526 StartZ=0 EndX=197.068 EndY=-91.935 EndZ=0
    g309: LineSegment StartX=197.068 StartY=-91.935 StartZ=0 EndX=197.022 EndY=-91.9197 EndZ=0
    g310: LineSegment StartX=197.022 StartY=-91.9197 StartZ=0 EndX=196.975 EndY=-91.9066 EndZ=0
    g311: LineSegment StartX=196.975 StartY=-91.9066 StartZ=0 EndX=196.927 EndY=-91.8959 EndZ=0
    g312: LineSegment StartX=196.927 StartY=-91.8959 StartZ=0 EndX=196.879 EndY=-91.8874 EndZ=0
    g313: LineSegment StartX=196.879 StartY=-91.8874 StartZ=0 EndX=196.83 EndY=-91.8814 EndZ=0
    g314: LineSegment StartX=196.83 StartY=-91.8814 StartZ=0 EndX=196.781 EndY=-91.8777 EndZ=0
    g315: LineSegment StartX=196.781 StartY=-91.8777 StartZ=0 EndX=196.731 EndY=-91.8765 EndZ=0
    g316: LineSegment StartX=196.731 StartY=-91.8765 StartZ=0 EndX=186.567 EndY=-91.8765 EndZ=0
    g317: LineSegment StartX=186.567 StartY=-91.8765 StartZ=0 EndX=186.516 EndY=-91.8778 EndZ=0
    g318: LineSegment StartX=186.516 StartY=-91.8778 StartZ=0 EndX=186.465 EndY=-91.8817 EndZ=0
    g319: LineSegment StartX=186.465 StartY=-91.8817 StartZ=0 EndX=186.415 EndY=-91.8881 EndZ=0
    g320: LineSegment StartX=186.415 StartY=-91.8881 StartZ=0 EndX=186.366 EndY=-91.8969 EndZ=0
    g321: LineSegment StartX=186.366 StartY=-91.8969 StartZ=0 EndX=186.318 EndY=-91.908 EndZ=0
    g322: LineSegment StartX=186.318 StartY=-91.908 StartZ=0 EndX=186.27 EndY=-91.9215 EndZ=0
    g323: LineSegment StartX=186.27 StartY=-91.9215 StartZ=0 EndX=186.224 EndY=-91.9372 EndZ=0
    g324: LineSegment StartX=186.224 StartY=-91.9372 StartZ=0 EndX=186.178 EndY=-91.9551 EndZ=0
    g325: LineSegment StartX=186.178 StartY=-91.9551 StartZ=0 EndX=186.134 EndY=-91.9752 EndZ=0
    g326: LineSegment StartX=186.134 StartY=-91.9752 StartZ=0 EndX=186.091 EndY=-91.9972 EndZ=0
    g327: LineSegment StartX=186.091 StartY=-91.9972 StartZ=0 EndX=186.049 EndY=-92.0213 EndZ=0
    g328: LineSegment StartX=186.049 StartY=-92.0213 StartZ=0 EndX=186.008 EndY=-92.0473 EndZ=0
    g329: LineSegment StartX=186.008 StartY=-92.0473 StartZ=0 EndX=185.969 EndY=-92.0752 EndZ=0
    g330: LineSegment StartX=185.969 StartY=-92.0752 StartZ=0 EndX=185.931 EndY=-92.1049 EndZ=0
    g331: LineSegment StartX=185.931 StartY=-92.1049 StartZ=0 EndX=185.895 EndY=-92.1363 EndZ=0
    g332: LineSegment StartX=185.895 StartY=-92.1363 StartZ=0 EndX=185.86 EndY=-92.1694 EndZ=0
    g333: LineSegment StartX=185.86 StartY=-92.1694 StartZ=0 EndX=185.827 EndY=-92.2042 EndZ=0
    g334: LineSegment StartX=185.827 StartY=-92.2042 StartZ=0 EndX=185.796 EndY=-92.2404 EndZ=0
    g335: LineSegment StartX=185.796 StartY=-92.2404 StartZ=0 EndX=185.766 EndY=-92.2782 EndZ=0
    g336: LineSegment StartX=185.766 StartY=-92.2782 StartZ=0 EndX=185.738 EndY=-92.3174 EndZ=0
    g337: LineSegment StartX=185.738 StartY=-92.3174 StartZ=0 EndX=185.712 EndY=-92.358 EndZ=0
    g338: LineSegment StartX=185.712 StartY=-92.358 StartZ=0 EndX=185.688 EndY=-92.3999 EndZ=0
    g339: LineSegment StartX=185.688 StartY=-92.3999 StartZ=0 EndX=185.666 EndY=-92.443 EndZ=0
    g340: LineSegment StartX=185.666 StartY=-92.443 StartZ=0 EndX=185.646 EndY=-92.4873 EndZ=0
    g341: LineSegment StartX=185.646 StartY=-92.4873 StartZ=0 EndX=185.628 EndY=-92.5327 EndZ=0
    g342: LineSegment StartX=185.628 StartY=-92.5327 StartZ=0 EndX=185.612 EndY=-92.5791 EndZ=0
    g343: LineSegment StartX=185.612 StartY=-92.5791 StartZ=0 EndX=185.599 EndY=-92.6266 EndZ=0
    g344: LineSegment StartX=185.599 StartY=-92.6266 StartZ=0 EndX=185.588 EndY=-92.675 EndZ=0
    g345: LineSegment StartX=185.588 StartY=-92.675 StartZ=0 EndX=185.579 EndY=-92.7242 EndZ=0
    g346: LineSegment StartX=185.579 StartY=-92.7242 StartZ=0 EndX=185.573 EndY=-92.7743 EndZ=0
    g347: LineSegment StartX=185.573 StartY=-92.7743 StartZ=0 EndX=185.569 EndY=-92.825 EndZ=0
    g348: LineSegment StartX=185.569 StartY=-92.825 StartZ=0 EndX=185.567 EndY=-92.8765 EndZ=0
    g349: LineSegment StartX=185.567 StartY=-92.8765 StartZ=0 EndX=185.567 EndY=-94.0446 EndZ=0
    g350: LineSegment StartX=185.567 StartY=-94.0446 StartZ=0 EndX=185.564 EndY=-94.199 EndZ=0
    g351: LineSegment StartX=185.564 StartY=-94.199 StartZ=0 EndX=185.552 EndY=-94.3514 EndZ=0
    g352: LineSegment StartX=185.552 StartY=-94.3514 StartZ=0 EndX=185.533 EndY=-94.5015 EndZ=0
    g353: LineSegment StartX=185.533 StartY=-94.5015 StartZ=0 EndX=185.506 EndY=-94.6492 EndZ=0
    g354: LineSegment StartX=185.506 StartY=-94.6492 StartZ=0 EndX=185.473 EndY=-94.7944 EndZ=0
    g355: LineSegment StartX=185.473 StartY=-94.7944 StartZ=0 EndX=185.433 EndY=-94.9367 EndZ=0
    g356: LineSegment StartX=185.433 StartY=-94.9367 StartZ=0 EndX=185.385 EndY=-95.0761 EndZ=0
    g357: LineSegment StartX=185.385 StartY=-95.0761 StartZ=0 EndX=185.332 EndY=-95.2123 EndZ=0
    g358: LineSegment StartX=185.332 StartY=-95.2123 StartZ=0 EndX=185.272 EndY=-95.3452 EndZ=0
    g359: LineSegment StartX=185.272 StartY=-95.3452 StartZ=0 EndX=185.205 EndY=-95.4746 EndZ=0
    g360: LineSegment StartX=185.205 StartY=-95.4746 StartZ=0 EndX=185.133 EndY=-95.6002 EndZ=0
    g361: LineSegment StartX=185.133 StartY=-95.6002 StartZ=0 EndX=185.055 EndY=-95.7219 EndZ=0
    g362: LineSegment StartX=185.055 StartY=-95.7219 StartZ=0 EndX=184.971 EndY=-95.8395 EndZ=0
    g363: LineSegment StartX=184.971 StartY=-95.8395 StartZ=0 EndX=184.882 EndY=-95.9529 EndZ=0
    g364: LineSegment StartX=184.882 StartY=-95.9529 StartZ=0 EndX=184.788 EndY=-96.0617 EndZ=0
    g365: LineSegment StartX=184.788 StartY=-96.0617 StartZ=0 EndX=184.689 EndY=-96.1659 EndZ=0
    g366: LineSegment StartX=184.689 StartY=-96.1659 StartZ=0 EndX=184.585 EndY=-96.2652 EndZ=0
    g367: LineSegment StartX=184.585 StartY=-96.2652 StartZ=0 EndX=184.476 EndY=-96.3595 EndZ=0
    g368: LineSegment StartX=184.476 StartY=-96.3595 StartZ=0 EndX=184.362 EndY=-96.4486 EndZ=0
    g369: LineSegment StartX=184.362 StartY=-96.4486 StartZ=0 EndX=184.245 EndY=-96.5322 EndZ=0
    g370: LineSegment StartX=184.245 StartY=-96.5322 StartZ=0 EndX=184.123 EndY=-96.6103 EndZ=0
    g371: LineSegment StartX=184.123 StartY=-96.6103 StartZ=0 EndX=183.997 EndY=-96.6825 EndZ=0
    g372: LineSegment StartX=183.997 StartY=-96.6825 StartZ=0 EndX=183.868 EndY=-96.7488 EndZ=0
    g373: LineSegment StartX=183.868 StartY=-96.7488 StartZ=0 EndX=183.735 EndY=-96.8088 EndZ=0
    g374: LineSegment StartX=183.735 StartY=-96.8088 StartZ=0 EndX=183.599 EndY=-96.8625 EndZ=0
    g375: LineSegment StartX=183.599 StartY=-96.8625 StartZ=0 EndX=183.46 EndY=-96.9097 EndZ=0
    g376: LineSegment StartX=183.46 StartY=-96.9097 StartZ=0 EndX=183.317 EndY=-96.9501 EndZ=0
    g377: LineSegment StartX=183.317 StartY=-96.9501 StartZ=0 EndX=183.172 EndY=-96.9836 EndZ=0
    g378: LineSegment StartX=183.172 StartY=-96.9836 StartZ=0 EndX=183.024 EndY=-97.01 EndZ=0
    g379: LineSegment StartX=183.024 StartY=-97.01 StartZ=0 EndX=182.874 EndY=-97.0291 EndZ=0
    g380: LineSegment StartX=182.874 StartY=-97.0291 StartZ=0 EndX=182.722 EndY=-97.0407 EndZ=0
    g381: LineSegment StartX=182.722 StartY=-97.0407 StartZ=0 EndX=182.567 EndY=-97.0446 EndZ=0
    g382: LineSegment StartX=182.567 StartY=-97.0446 StartZ=0 EndX=116.07 EndY=-97.0446 EndZ=0
    g383: LineSegment StartX=116.07 StartY=-97.0446 StartZ=0 EndX=102.371 EndY=-98.9778 EndZ=0
    g384: LineSegment StartX=102.371 StartY=-98.9778 StartZ=0 EndX=102.259 EndY=-98.9948 EndZ=0
    g385: LineSegment StartX=102.259 StartY=-98.9948 StartZ=0 EndX=102.148 EndY=-99.0143 EndZ=0
    g386: LineSegment StartX=102.148 StartY=-99.0143 StartZ=0 EndX=102.038 EndY=-99.0363 EndZ=0
    g387: LineSegment StartX=102.038 StartY=-99.0363 StartZ=0 EndX=101.928 EndY=-99.0608 EndZ=0
    g388: LineSegment StartX=101.928 StartY=-99.0608 StartZ=0 EndX=101.819 EndY=-99.0877 EndZ=0
    g389: LineSegment StartX=101.819 StartY=-99.0877 StartZ=0 EndX=101.71 EndY=-99.117 EndZ=0
    g390: LineSegment StartX=101.71 StartY=-99.117 StartZ=0 EndX=101.603 EndY=-99.1488 EndZ=0
    g391: LineSegment StartX=101.603 StartY=-99.1488 StartZ=0 EndX=101.495 EndY=-99.183 EndZ=0
    g392: LineSegment StartX=101.495 StartY=-99.183 StartZ=0 EndX=101.389 EndY=-99.2196 EndZ=0
    g393: LineSegment StartX=101.389 StartY=-99.2196 StartZ=0 EndX=101.284 EndY=-99.2585 EndZ=0
    g394: LineSegment StartX=101.284 StartY=-99.2585 StartZ=0 EndX=101.179 EndY=-99.2999 EndZ=0
    g395: LineSegment StartX=101.179 StartY=-99.2999 StartZ=0 EndX=101.076 EndY=-99.3436 EndZ=0
    g396: LineSegment StartX=101.076 StartY=-99.3436 StartZ=0 EndX=100.973 EndY=-99.3896 EndZ=0
    g397: LineSegment StartX=100.973 StartY=-99.3896 StartZ=0 EndX=100.871 EndY=-99.438 EndZ=0
    g398: LineSegment StartX=100.871 StartY=-99.438 StartZ=0 EndX=100.77 EndY=-99.4887 EndZ=0
    g399: LineSegment StartX=100.77 StartY=-99.4887 StartZ=0 EndX=100.671 EndY=-99.5417 EndZ=0
    ... +104 more geometry lines
  constraints (504):
    c: Coincident(g437,g438)
    c: Coincident(g438,g439)
    c: Coincident(g439,g440)
    c: Coincident(g436,g437)
    c: Coincident(g440,g441)
    c: Coincident(g435,g436)
    c: Coincident(g441,g442)
    c: Coincident(g434,g435)
    c: Coincident(g442,g443)
    c: Coincident(g433,g434)
    c: Coincident(g443,g444)
    c: Coincident(g432,g433)
    c: Coincident(g444,g445)
    c: Coincident(g431,g432)
    c: Coincident(g445,g446)
    c: Coincident(g430,g431)
    c: Coincident(g446,g447)
    c: Coincident(g429,g430)
    c: Coincident(g447,g448)
    c: Coincident(g428,g429)
    c: Coincident(g448,g449)
    c: Coincident(g427,g428)
    c: Coincident(g449,g450)
    c: Coincident(g426,g427)
    c: Coincident(g425,g426)
    c: Coincident(g424,g425)
    c: Coincident(g423,g424)
    c: Coincident(g422,g423)
    c: Coincident(g421,g422)
    c: Coincident(g420,g421)
    c: Coincident(g419,g420)
    c: Coincident(g418,g419)
    c: Coincident(g417,g418)
    c: Coincident(g450,g451)
    c: Coincident(g451,g452)
    c: Coincident(g452,g453)
    c: Coincident(g453,g454)
    c: Coincident(g454,g455)
    c: Coincident(g455,g456)
    c: Coincident(g456,g457)
    c: Coincident(g457,g458)
    c: Coincident(g458,g459)
    c: Coincident(g459,g460)
    c: Coincident(g460,g461)
    c: Coincident(g461,g462)
    c: Coincident(g462,g463)
    c: Coincident(g463,g464)
    c: Coincident(g464,g465)
    c: Coincident(g465,g466)
    c: Coincident(g466,g467)
    c: Coincident(g467,g468)
    c: Coincident(g468,g469)
    c: Coincident(g469,g470)
    c: Coincident(g470,g471)
    c: Coincident(g471,g472)
    c: Coincident(g472,g473)
    c: Coincident(g473,g474)
    c: Coincident(g474,g475)
    c: Coincident(g475,g476)
    c: Coincident(g476,g477)
    c: Coincident(g477,g478)
    c: Coincident(g478,g479)
    c: Coincident(g479,g480)
    c: Coincident(g480,g481)
    c: Coincident(g481,g482)
    c: Coincident(g482,g483)
    c: Coincident(g483,g484)
    c: Coincident(g484,g485)
    c: Coincident(g416,g417)
    c: Coincident(g485,g486)
    c: Coincident(g415,g416)
    c: Coincident(g414,g415)
    c: Coincident(g486,g487)
    c: Coincident(g413,g414)
    c: Coincident(g487,g488)
    c: Coincident(g412,g413)
    c: Coincident(g411,g412)
    c: Coincident(g488,g489)
    c: Coincident(g410,g411)
    c: Coincident(g489,g490)
    c: Coincident(g409,g410)
    c: Coincident(g408,g409)
    c: Coincident(g490,g491)
    c: Coincident(g407,g408)
    c: Coincident(g406,g407)
    c: Coincident(g491,g492)
    c: Coincident(g405,g406)
    c: Coincident(g492,g493)
    c: Coincident(g404,g405)
    c: Coincident(g403,g404)
    c: Coincident(g493,g494)
    c: Coincident(g402,g403)
    c: Coincident(g401,g402)
    c: Coincident(g494,g495)
    c: Coincident(g400,g401)
    c: Coincident(g495,g496)
    c: Coincident(g496,g497)
    c: Coincident(g497,g498)
    c: Coincident(g498,g499)
    c: Coincident(g499,g500)
    c: Coincident(g399,g400)
    c: Coincident(g398,g399)
    c: Coincident(g397,g398)
    c: Coincident(g396,g397)
    c: Coincident(g395,g396)
    c: Coincident(g394,g395)
    c: Coincident(g393,g394)
    c: Coincident(g392,g393)
    c: Coincident(g391,g392)
    c: Coincident(g390,g391)
    c: Coincident(g389,g390)
    c: Coincident(g388,g389)
    c: Coincident(g387,g388)
    c: Coincident(g386,g387)
    c: Coincident(g385,g386)
    c: Coincident(g384,g385)
    c: Coincident(g383,g384)
    c: Coincident(g382,g383)
    c: Coincident(g500,g501)
    c: Coincident(g501,g502)
    c: Coincident(g502,g503)
    c: Coincident(g96,g97)
    c: Coincident(g97,g98)
    c: Coincident(g95,g96)
    c: Coincident(g98,g99)
    c: Coincident(g99,g100)
    c: Coincident(g94,g95)
    c: Coincident(g100,g101)
    c: Coincident(g93,g94)
    c: Coincident(g101,g102)
    c: Coincident(g92,g93)
    c: Coincident(g102,g103)
    c: Coincident(g91,g92)
    c: Coincident(g103,g104)
    c: Coincident(g90,g91)
    c: Coincident(g104,g105)
    c: Coincident(g89,g90)
    c: Coincident(g105,g106)
    c: Coincident(g88,g89)
    c: Coincident(g106,g107)
    c: Coincident(g87,g88)
    c: Coincident(g107,g108)
    c: Coincident(g86,g87)
    c: Coincident(g108,g109)
    c: Coincident(g85,g86)
    c: Coincident(g109,g110)
    c: Coincident(g84,g85)
    c: Coincident(g110,g111)
    c: Coincident(g83,g84)
    c: Coincident(g111,g112)
    c: Coincident(g82,g83)
    c: Coincident(g112,g113)
    c: Coincident(g81,g82)
    c: Coincident(g113,g114)
    c: Coincident(g80,g81)
    c: Coincident(g114,g115)
    c: Coincident(g79,g80)
    c: Coincident(g115,g116)
    c: Coincident(g78,g79)
    c: Coincident(g116,g117)
    c: Coincident(g77,g78)
    c: Coincident(g117,g118)
    c: Coincident(g76,g77)
    c: Coincident(g118,g119)
    c: Coincident(g75,g76)
    c: Coincident(g119,g120)
    c: Coincident(g74,g75)
    c: Coincident(g120,g121)
    c: Coincident(g73,g74)
    c: Coincident(g121,g122)
    c: Coincident(g72,g73)
    c: Coincident(g122,g123)
    c: Coincident(g71,g72)
    c: Coincident(g123,g124)
    c: Coincident(g70,g71)
    c: Coincident(g124,g125)
    c: Coincident(g69,g70)
    c: Coincident(g125,g126)
    c: Coincident(g68,g69)
    c: Coincident(g126,g127)
    c: Coincident(g67,g68)
    c: Coincident(g127,g128)
    c: Coincident(g66,g67)
    c: Coincident(g128,g129)
    c: Coincident(g65,g66)
    c: Coincident(g0,g129)
    c: Coincident(g64,g65)
    c: Coincident(g0,g1)
    c: Coincident(g63,g64)
    c: Coincident(g1,g2)
    c: Coincident(g62,g63)
    c: Coincident(g2,g3)
    c: Coincident(g61,g62)
    c: Coincident(g3,g4)
    c: Coincident(g60,g61)
    c: Coincident(g4,g5)
    c: Coincident(g59,g60)
    c: Coincident(g5,g6)
    c: Coincident(g58,g59)
    c: Coincident(g6,g7)
    c: Coincident(g57,g58)
    c: Coincident(g7,g8)
    c: Coincident(g56,g57)
    c: Coincident(g8,g9)
    c: Coincident(g55,g56)
    c: Coincident(g9,g10)
    c: Coincident(g54,g55)
    c: Coincident(g10,g11)
    c: Coincident(g53,g54)
    c: Coincident(g11,g12)
    c: Coincident(g52,g53)
    c: Coincident(g12,g13)
    c: Coincident(g51,g52)
    c: Coincident(g13,g14)
    c: Coincident(g50,g51)
    c: Coincident(g14,g15)
    c: Coincident(g49,g50)
    c: Coincident(g15,g16)
    c: Coincident(g48,g49)
    c: Coincident(g16,g17)
    c: Coincident(g47,g48)
    c: Coincident(g17,g18)
    c: Coincident(g46,g47)
    c: Coincident(g18,g19)
    c: Coincident(g45,g46)
    c: Coincident(g19,g20)
    c: Coincident(g44,g45)
    c: Coincident(g20,g21)
    c: Coincident(g43,g44)
    c: Coincident(g21,g22)
    c: Coincident(g42,g43)
    c: Coincident(g22,g23)
    c: Coincident(g41,g42)
    c: Coincident(g23,g24)
    c: Coincident(g40,g41)
    c: Coincident(g24,g25)
    c: Coincident(g39,g40)
    c: Coincident(g25,g26)
    c: Coincident(g38,g39)
    c: Coincident(g26,g27)
    c: Coincident(g37,g38)
    c: Coincident(g27,g28)
    c: Coincident(g36,g37)
    c: Coincident(g28,g29)
    c: Coincident(g35,g36)
    c: Coincident(g29,g30)
    c: Coincident(g34,g35)
    c: Coincident(g33,g34)
    c: Coincident(g31,g32)
    c: Coincident(g30,g31)
    c: Coincident(g32,g33)
    c: Coincident(g381,g382)
    c: Coincident(g380,g381)
    c: Coincident(g379,g380)
    c: Coincident(g378,g379)
    c: Coincident(g377,g378)
    c: Coincident(g376,g377)
    c: Coincident(g375,g376)
    c: Coincident(g374,g375)
    c: Coincident(g373,g374)
    c: Coincident(g372,g373)
    c: Coincident(g371,g372)
    c: Coincident(g370,g371)
    c: Coincident(g369,g370)
    c: Coincident(g368,g369)
    c: Coincident(g367,g368)
    c: Coincident(g366,g367)
    c: Coincident(g365,g366)
    c: Coincident(g364,g365)
    c: Coincident(g363,g364)
    c: Coincident(g362,g363)
    c: Coincident(g361,g362)
    c: Coincident(g360,g361)
    c: Coincident(g359,g360)
    c: Coincident(g358,g359)
    c: Coincident(g357,g358)
    c: Coincident(g356,g357)
    c: Coincident(g355,g356)
    c: Coincident(g354,g355)
    c: Coincident(g353,g354)
    c: Coincident(g352,g353)
    c: Coincident(g351,g352)
    c: Coincident(g350,g351)
    c: Coincident(g349,g350)
    c: Coincident(g348,g349)
    c: Coincident(g347,g348)
    c: Coincident(g346,g347)
    c: Coincident(g345,g346)
    c: Coincident(g344,g345)
    c: Coincident(g343,g344)
    c: Coincident(g342,g343)
    c: Coincident(g341,g342)
    c: Coincident(g340,g341)
    c: Coincident(g339,g340)
    c: Coincident(g338,g339)
    c: Coincident(g337,g338)
    c: Coincident(g336,g337)
    c: Coincident(g335,g336)
    c: Coincident(g334,g335)
    c: Coincident(g333,g334)
    c: Coincident(g332,g333)
    c: Coincident(g331,g332)
    c: Coincident(g330,g331)
    c: Coincident(g329,g330)
    c: Coincident(g328,g329)
    c: Coincident(g327,g328)
    c: Coincident(g326,g327)
    c: Coincident(g325,g326)
    c: Coincident(g324,g325)
    c: Coincident(g323,g324)
    c: Coincident(g322,g323)
    c: Coincident(g321,g322)
    c: Coincident(g320,g321)
    c: Coincident(g319,g320)
    c: Coincident(g318,g319)
    c: Coincident(g317,g318)
    c: Coincident(g316,g317)
    c: Coincident(g130,g503)
    c: Coincident(g315,g316)
    c: Coincident(g314,g315)
    c: Coincident(g313,g314)
    c: Coincident(g312,g313)
    c: Coincident(g311,g312)
    c: Coincident(g310,g311)
    c: Coincident(g309,g310)
    c: Coincident(g308,g309)
    c: Coincident(g307,g308)
    c: Coincident(g306,g307)
    c: Coincident(g305,g306)
    c: Coincident(g304,g305)
    c: Coincident(g303,g304)
    c: Coincident(g302,g303)
    c: Coincident(g301,g302)
    c: Coincident(g300,g301)
    c: Coincident(g299,g300)
    c: Coincident(g298,g299)
    c: Coincident(g297,g298)
    c: Coincident(g296,g297)
    c: Coincident(g295,g296)
    c: Coincident(g294,g295)
    c: Coincident(g293,g294)
    c: Coincident(g292,g293)
    c: Coincident(g291,g292)
    c: Coincident(g290,g291)
    c: Coincident(g289,g290)
    c: Coincident(g288,g289)
    c: Coincident(g287,g288)
    c: Coincident(g281,g282)
    c: Coincident(g282,g283)
    c: Coincident(g283,g284)
    c: Coincident(g284,g285)
    c: Coincident(g285,g286)
    c: Coincident(g286,g287)
    c: Coincident(g280,g281)
    c: Coincident(g279,g280)
    c: Coincident(g278,g279)
    c: Coincident(g277,g278)
    c: Coincident(g276,g277)
    c: Coincident(g275,g276)
    c: Coincident(g274,g275)
    c: Coincident(g273,g274)
    c: Coincident(g272,g273)
    c: Coincident(g271,g272)
    c: Coincident(g270,g271)
    c: Coincident(g269,g270)
    c: Coincident(g268,g269)
    c: Coincident(g267,g268)
    c: Coincident(g266,g267)
    c: Coincident(g265,g266)
    c: Coincident(g264,g265)
    c: Coincident(g263,g264)
    c: Coincident(g262,g263)
    c: Coincident(g261,g262)
    c: Coincident(g260,g261)
    c: Coincident(g259,g260)
    c: Coincident(g258,g259)
    c: Coincident(g257,g258)
    c: Coincident(g256,g257)
    c: Coincident(g255,g256)
    c: Coincident(g254,g255)
    c: Coincident(g131,g132)
    c: Coincident(g130,g131)
    c: Coincident(g253,g254)
    c: Coincident(g252,g253)
    c: Coincident(g251,g252)
    c: Coincident(g250,g251)
    c: Coincident(g249,g250)
    c: Coincident(g248,g249)
    c: Coincident(g247,g248)
    c: Coincident(g246,g247)
    c: Coincident(g245,g246)
    c: Coincident(g244,g245)
    c: Coincident(g243,g244)
    c: Coincident(g242,g243)
    c: Coincident(g241,g242)
    c: Coincident(g240,g241)
    c: Coincident(g239,g240)
    c: Coincident(g238,g239)
    c: Coincident(g237,g238)
    c: Coincident(g236,g237)
    c: Coincident(g235,g236)
    c: Coincident(g234,g235)
    c: Coincident(g233,g234)
    c: Coincident(g232,g233)
    c: Coincident(g132,g133)
    c: Coincident(g133,g134)
    c: Coincident(g134,g135)
    c: Coincident(g135,g136)
    c: Coincident(g136,g137)
    c: Coincident(g231,g232)
    c: Coincident(g137,g138)
    c: Coincident(g230,g231)
    c: Coincident(g229,g230)
    c: Coincident(g138,g139)
    c: Coincident(g228,g229)
    c: Coincident(g139,g140)
    c: Coincident(g227,g228)
    c: Coincident(g226,g227)
    c: Coincident(g140,g141)
    c: Coincident(g225,g226)
    c: Coincident(g224,g225)
    c: Coincident(g141,g142)
    c: Coincident(g223,g224)
    c: Coincident(g142,g143)
    c: Coincident(g222,g223)
    c: Coincident(g221,g222)
    c: Coincident(g143,g144)
    c: Coincident(g220,g221)
    c: Coincident(g219,g220)
    c: Coincident(g144,g145)
    c: Coincident(g218,g219)
    c: Coincident(g145,g146)
    c: Coincident(g217,g218)
    c: Coincident(g216,g217)
    c: Coincident(g146,g147)
    c: Coincident(g215,g216)
    c: Coincident(g147,g148)
    c: Coincident(g148,g149)
    c: Coincident(g149,g150)
    c: Coincident(g150,g151)
    c: Coincident(g151,g152)
    c: Coincident(g152,g153)
    c: Coincident(g153,g154)
    c: Coincident(g154,g155)
    c: Coincident(g155,g156)
    c: Coincident(g156,g157)
    c: Coincident(g157,g158)
    c: Coincident(g158,g159)
    c: Coincident(g159,g160)
    c: Coincident(g160,g161)
    c: Coincident(g161,g162)
    c: Coincident(g162,g163)
    c: Coincident(g163,g164)
    c: Coincident(g168,g169)
    c: Coincident(g167,g168)
    c: Coincident(g166,g167)
    c: Coincident(g165,g166)
    c: Coincident(g164,g165)
    c: Coincident(g169,g170)
    c: Coincident(g170,g171)
    c: Coincident(g171,g172)
    c: Coincident(g172,g173)
    c: Coincident(g173,g174)
    c: Coincident(g174,g175)
    c: Coincident(g175,g176)
    c: Coincident(g176,g177)
    c: Coincident(g177,g178)
    c: Coincident(g178,g179)
    c: Coincident(g179,g180)
    c: Coincident(g180,g181)
    c: Coincident(g181,g182)
    c: Coincident(g214,g215)
    c: Coincident(g213,g214)
    c: Coincident(g212,g213)
    c: Coincident(g211,g212)
    c: Coincident(g210,g211)
    c: Coincident(g209,g210)
    c: Coincident(g208,g209)
    c: Coincident(g207,g208)
    c: Coincident(g206,g207)
    c: Coincident(g205,g206)
    c: Coincident(g182,g183)
    c: Coincident(g204,g205)
    c: Coincident(g183,g184)
    c: Coincident(g203,g204)
    c: Coincident(g184,g185)
    c: Coincident(g202,g203)
    c: Coincident(g185,g186)
    c: Coincident(g201,g202)
    c: Coincident(g186,g187)
    c: Coincident(g200,g201)
    c: Coincident(g187,g188)
    c: Coincident(g199,g200)
    c: Coincident(g188,g189)
    c: Coincident(g198,g199)
    c: Coincident(g197,g198)
    c: Coincident(g189,g190)
    c: Coincident(g196,g197)
    c: Coincident(g190,g191)
    c: Coincident(g195,g196)
    c: Coincident(g191,g192)
    c: Coincident(g194,g195)
    c: Coincident(g193,g194)
    c: Coincident(g192,g193)
FEATURE [App::Part] Board_Geoms_514c
  Group = -> [Pcb_514c,PCB_Sketch_514c]
  Origin = -> Origin002
FEATURE [App::Part] Step_Models_514c
  Origin = -> Origin004
FEATURE [App::Part] Board_514c  label="MilkTastic"
  Group = -> [Local_CS_514c,Board_Geoms_514c,Step_Models_514c]
  Origin = -> Origin003
FEATURE [PartDesign::ShapeBinder] ShapeBinder
  Support = -> [Pcb_514c]
  TraceSupport = false
FEATURE [Sketcher::SketchObject] Sketch
  ExternalGeometry = -> [ShapeBinder]
  FullyConstrained = false
  MapMode = 5
  Support = -> [XY_Plane001]
  sketch-geometry (81):
    g0: LineSegment StartX=86.5696 StartY=-30.1929 StartZ=0 EndX=116.57 EndY=-30.1929 EndZ=0
    g1: LineSegment StartX=116.57 StartY=-30.1929 StartZ=0 EndX=116.57 EndY=-26.9154 EndZ=0
    g2: LineSegment StartX=116.57 StartY=-26.9154 StartZ=0 EndX=128.57 EndY=-23.4173 EndZ=0
    g3: LineSegment StartX=128.57 StartY=-23.4173 StartZ=0 EndX=188.25 EndY=-23.4173 EndZ=0
    g4: LineSegment StartX=188.25 StartY=-23.4173 StartZ=0 EndX=200.25 EndY=-26.9154 EndZ=0
    g5: LineSegment StartX=200.25 StartY=-26.9154 StartZ=0 EndX=200.25 EndY=-30.1929 EndZ=0
    g6: LineSegment StartX=200.25 StartY=-30.1929 StartZ=0 EndX=230.25 EndY=-30.1929 EndZ=0
    g7: LineSegment StartX=230.25 StartY=-30.1929 StartZ=0 EndX=230.338 EndY=-30.1929 EndZ=0
    g8: LineSegment StartX=240.25 StartY=-40.1046 StartZ=0 EndX=240.25 EndY=-40.1929 EndZ=0
    g9: LineSegment StartX=240.603 StartY=-72.9933 StartZ=0 EndX=240.603 EndY=-72.9933 EndZ=0
    g10: LineSegment StartX=252.704 StartY=-93.3529 StartZ=0 EndX=252.795 EndY=-93.4529 EndZ=0
    g11: LineSegment StartX=252.853 StartY=-97.2603 StartZ=0 EndX=251.523 EndY=-98.8101 EndZ=0
    g12: LineSegment StartX=251.523 StartY=-98.8101 StartZ=0 EndX=236.753 EndY=-108.411 EndZ=0
    g13: LineSegment StartX=236.753 StartY=-108.411 StartZ=0 EndX=235.162 EndY=-110.071 EndZ=0
    g14: LineSegment StartX=234.635 StartY=-110.109 StartZ=0 EndX=232.654 EndY=-108.567 EndZ=0
    g15: LineSegment StartX=232.654 StartY=-108.567 StartZ=0 EndX=216.148 EndY=-99.5417 EndZ=0
    g16: LineSegment StartX=216.148 StartY=-99.5417 StartZ=0 EndX=215.454 EndY=-99.0138 EndZ=0
    g17: LineSegment StartX=215.347 StartY=-98.9778 StartZ=0 EndX=214.448 EndY=-98.9778 EndZ=0
    g18: LineSegment StartX=214.448 StartY=-98.9778 StartZ=0 EndX=200.75 EndY=-97.0446 EndZ=0
    g19: LineSegment StartX=200.75 StartY=-97.0446 StartZ=0 EndX=198.899 EndY=-96.7496 EndZ=0
    g20: LineSegment StartX=198.766 StartY=-96.655 StartZ=0 EndX=198.32 EndY=-95.8294 EndZ=0
    g21: LineSegment StartX=198.32 StartY=-95.8294 StartZ=0 EndX=197.878 EndY=-95.0913 EndZ=0
    g22: LineSegment StartX=197.855 StartY=-95.0231 StartZ=0 EndX=197.731 EndY=-94.0446 EndZ=0
    g23: LineSegment StartX=197.731 StartY=-94.0446 StartZ=0 EndX=197.731 EndY=-92.8765 EndZ=0
    g24: LineSegment StartX=197.731 StartY=-92.8765 StartZ=0 EndX=197.731 EndY=-92.0179 EndZ=0
    g25: LineSegment StartX=197.59 StartY=-91.8765 StartZ=0 EndX=196.731 EndY=-91.8765 EndZ=0
    g26: LineSegment StartX=196.731 StartY=-91.8765 StartZ=0 EndX=186.567 EndY=-91.8765 EndZ=0
    g27: LineSegment StartX=186.567 StartY=-91.8765 StartZ=0 EndX=185.624 EndY=-91.925 EndZ=0
    g28: LineSegment StartX=185.5 StartY=-92.0677 StartZ=0 EndX=185.567 EndY=-92.8765 EndZ=0
    g29: LineSegment StartX=185.567 StartY=-92.8765 StartZ=0 EndX=185.516 EndY=-94.1939 EndZ=0
    g30: LineSegment StartX=185.516 StartY=-94.1939 StartZ=0 EndX=185.516 EndY=-96.6415 EndZ=0
    g31: LineSegment StartX=185.113 StartY=-97.0446 StartZ=0 EndX=182.567 EndY=-97.0446 EndZ=0
    g32: LineSegment StartX=182.567 StartY=-97.0446 StartZ=0 EndX=116.07 EndY=-97.0446 EndZ=0
    g33: LineSegment StartX=116.07 StartY=-97.0446 StartZ=0 EndX=102.371 EndY=-98.9778 EndZ=0
    g34: LineSegment StartX=102.371 StartY=-98.9778 StartZ=0 EndX=101.36 EndY=-99.0995 EndZ=0
    g35: LineSegment StartX=101.293 StartY=-99.1243 StartZ=0 EndX=100.671 EndY=-99.5417 EndZ=0
    g36: LineSegment StartX=100.671 StartY=-99.5417 StartZ=0 EndX=84.1657 EndY=-108.567 EndZ=0
    g37: LineSegment StartX=84.1657 StartY=-108.567 StartZ=0 EndX=82.296 EndY=-109.399 EndZ=0
    g38: LineSegment StartX=81.9453 StartY=-109.388 StartZ=0 EndX=80.0668 EndY=-108.411 EndZ=0
    g39: LineSegment StartX=80.0668 StartY=-108.411 StartZ=0 EndX=65.2965 EndY=-98.8101 EndZ=0
    g40: LineSegment StartX=65.2965 StartY=-98.8101 StartZ=0 EndX=63.0644 EndY=-97.0029 EndZ=0
    g41: LineSegment StartX=62.9032 StartY=-96.4062 StartZ=0 EndX=64.0411 EndY=-93.4073 EndZ=0
    g42: LineSegment StartX=64.0411 StartY=-93.4073 StartZ=0 EndX=76.2168 EndY=-72.9933 EndZ=0
    g43: LineSegment StartX=76.2168 StartY=-72.9933 StartZ=0 EndX=76.5499 EndY=-72.4716 EndZ=0
    g44: LineSegment StartX=76.5697 StartY=-72.4038 StartZ=0 EndX=76.5697 EndY=-71.7127 EndZ=0
    g45: LineSegment StartX=76.5697 StartY=-71.7127 StartZ=0 EndX=76.5697 EndY=-40.1929 EndZ=0
    g46: LineSegment StartX=76.5697 StartY=-40.1929 StartZ=0 EndX=76.5697 EndY=-40.1457 EndZ=0
    g47: LineSegment StartX=86.5225 StartY=-30.1929 StartZ=0 EndX=86.5696 EndY=-30.1929 EndZ=0
    g48: ArcOfCircle CenterX=86.5225 CenterY=-40.1457 CenterZ=0 NormalX=0 NormalY=0 NormalZ=1 AngleXU=0 Radius=9.95281 StartAngle=1.5708 EndAngle=3.14159
    g49: GeomPoint X=76.5697 Y=-30.1929 Z=0
    g50: ArcOfCircle CenterX=230.338 CenterY=-40.1046 CenterZ=0 NormalX=0 NormalY=0 NormalZ=1 AngleXU=0 Radius=9.9117 StartAngle=2e-16 EndAngle=1.5708
    g51: GeomPoint X=240.25 Y=-30.1929 Z=0
    g52: GeomPoint X=240.244 Y=-72.5789 Z=0
    g53: ArcOfCircle CenterX=250.672 CenterY=-95.3893 CenterZ=0 NormalX=0 NormalY=0 NormalZ=1 AngleXU=0 Radius=2.87322 StartAngle=5.57404 EndAngle=7.02269
    g54: GeomPoint X=254.508 Y=-95.331 Z=0
    g55: ArcOfCircle CenterX=234.877 CenterY=-109.798 CenterZ=0 NormalX=0 NormalY=0 NormalZ=1 AngleXU=0 Radius=0.39427 StartAngle=4.05069 EndAngle=5.5191
    g56: GeomPoint X=234.915 Y=-110.328 Z=0
    g57: ArcOfCircle CenterX=215.347 CenterY=-99.1544 CenterZ=0 NormalX=0 NormalY=0 NormalZ=1 AngleXU=0 Radius=0.176646 StartAngle=0.920956 EndAngle=1.5708
    g58: GeomPoint X=215.406 Y=-98.9778 Z=0
    g59: ArcOfCircle CenterX=198.928 CenterY=-96.5673 CenterZ=0 NormalX=0 NormalY=0 NormalZ=1 AngleXU=0 Radius=0.184572 StartAngle=3.6366 EndAngle=4.55429
    g60: GeomPoint X=198.809 Y=-96.7352 Z=0
    g61: ArcOfCircle CenterX=198.029 CenterY=-95.0011 CenterZ=0 NormalX=0 NormalY=0 NormalZ=1 AngleXU=0 Radius=0.175582 StartAngle=3.26719 EndAngle=3.68071
    g62: GeomPoint X=197.859 Y=-95.0597 Z=0
    g63: ArcOfCircle CenterX=197.59 CenterY=-92.0179 CenterZ=0 NormalX=0 NormalY=0 NormalZ=1 AngleXU=0 Radius=0.141427 StartAngle=0 EndAngle=1.5708
    g64: GeomPoint X=197.731 Y=-91.8765 Z=0
    g65: ArcOfCircle CenterX=185.631 CenterY=-92.0566 CenterZ=0 NormalX=0 NormalY=0 NormalZ=1 AngleXU=0 Radius=0.13186 StartAngle=1.62209 EndAngle=3.2253
    g66: GeomPoint X=185.488 Y=-91.9319 Z=0
    g67: ArcOfCircle CenterX=185.113 CenterY=-96.6415 CenterZ=0 NormalX=0 NormalY=0 NormalZ=1 AngleXU=0 Radius=0.403144 StartAngle=4.71239 EndAngle=6.28319
    g68: GeomPoint X=185.516 Y=-97.0446 Z=0
    g69: ArcOfCircle CenterX=101.378 CenterY=-99.2512 CenterZ=0 NormalX=0 NormalY=0 NormalZ=1 AngleXU=0 Radius=0.152783 StartAngle=1.69053 EndAngle=2.16196
    g70: GeomPoint X=101.323 Y=-99.1038 Z=0
    g71: ArcOfCircle CenterX=82.1317 CenterY=-109.03 CenterZ=0 NormalX=0 NormalY=0 NormalZ=1 AngleXU=0 Radius=0.403775 StartAngle=4.23251 EndAngle=5.1313
    g72: GeomPoint X=82.1181 Y=-109.478 Z=0
    g73: ArcOfCircle CenterX=63.3961 CenterY=-96.5932 CenterZ=0 NormalX=0 NormalY=0 NormalZ=1 AngleXU=0 Radius=0.52714 StartAngle=2.77896 EndAngle=4.03179
    g74: GeomPoint X=62.7679 Y=-96.7629 Z=0
    g75: ArcOfCircle CenterX=76.4438 CenterY=-72.4038 CenterZ=0 NormalX=0 NormalY=0 NormalZ=1 AngleXU=0 Radius=0.125886 StartAngle=5.71491 EndAngle=6.28319
    g76: GeomPoint X=76.5697 Y=-72.4406 Z=0
    g77: LineSegment StartX=252.704 StartY=-93.3529 StartZ=0 EndX=240.586 EndY=-72.9378 EndZ=0
    g78: LineSegment StartX=240.25 StartY=-71.7127 StartZ=0 EndX=240.25 EndY=-40.1929 EndZ=0
    g79: ArcOfCircle CenterX=242.65 CenterY=-71.7127 CenterZ=0 NormalX=0 NormalY=0 NormalZ=1 AngleXU=0 Radius=2.40034 StartAngle=3.14159 EndAngle=3.67727
    g80: GeomPoint X=240.25 Y=-72.3714 Z=0
  constraints (139):
    c: Coincident(g-3,g0)
    c: Coincident(g0,g-3)
    c: Coincident(g0,g1)
    c: Coincident(g1,g-4)
    c: Coincident(g1,g2)
    c: Coincident(g2,g-5)
    c: Coincident(g2,g3)
    c: Coincident(g3,g-6)
    c: Coincident(g3,g4)
    c: Coincident(g4,g-6)
    c: Coincident(g4,g5)
    c: Coincident(g5,g-7)
    c: Coincident(g5,g6)
    c: Coincident(g6,g-7)
    c: Coincident(g6,g7)
    c: Horizontal(g7)
    c: Coincident(g8,g-8)
    c: Vertical(g8)
    c: Coincident(g9,g-9)
    c: Coincident(g11,g-10)
    c: Coincident(g11,g12)
    c: Coincident(g12,g-10)
    c: Coincident(g12,g13)
    c: Coincident(g14,g-11)
    c: Coincident(g14,g15)
    c: Coincident(g15,g-11)
    c: Coincident(g15,g16)
    c: Coincident(g17,g-12)
    c: Horizontal(g17)
    c: Coincident(g17,g18)
    c: Coincident(g18,g-12)
    c: Coincident(g18,g19)
    c: Coincident(g20,g-14)
    c: Coincident(g20,g21)
    c: Coincident(g22,g-15)
    c: Coincident(g22,g23)
    c: Coincident(g23,g-15)
    c: Coincident(g23,g24)
    c: Vertical(g24)
    c: Coincident(g25,g-13)
    c: Horizontal(g25)
    c: Coincident(g25,g26)
    c: Coincident(g26,g-13)
    c: Coincident(g26,g27)
    c: Coincident(g28,g-16)
    c: Coincident(g28,g29)
    c: Coincident(g29,g30)
    c: Vertical(g30)
    c: Coincident(g31,g-17)
    c: Horizontal(g31)
    c: Coincident(g31,g32)
    c: Coincident(g32,g-18)
    c: Coincident(g32,g33)
    c: Coincident(g33,g-18)
    c: Coincident(g33,g34)
    c: Coincident(g35,g-19)
    c: Coincident(g35,g36)
    c: Coincident(g36,g-19)
    c: Coincident(g36,g37)
    c: Coincident(g38,g-20)
    c: Coincident(g38,g39)
    c: Coincident(g39,g-20)
    c: Coincident(g39,g40)
    c: Coincident(g41,g-21)
    c: Coincident(g41,g42)
    c: Coincident(g42,g-21)
    c: Coincident(g42,g43)
    c: Coincident(g44,g-22)
    c: Vertical(g44)
    c: Coincident(g44,g45)
    c: Coincident(g45,g-22)
    c: Coincident(g45,g46)
    c: Vertical(g46)
    c: Coincident(g47,g0)
    c: Horizontal(g47)
    c: PointOnObject(g49,g46)
    c: PointOnObject(g49,g47)
    c: Tangent(g46,g48) = 1.5708
    c: Tangent(g47,g48) = 1.5708
    c: PointOnObject(g51,g7)
    c: PointOnObject(g51,g8)
    c: Tangent(g7,g50) = 1.5708
    c: Tangent(g8,g50) = 1.5708
    c: PointOnObject(g52,g9)
    c: PointOnObject(g54,g10)
    c: PointOnObject(g54,g11)
    c: Tangent(g10,g53) = 1.5708
    c: Tangent(g11,g53) = 1.5708
    c: PointOnObject(g56,g13)
    c: PointOnObject(g56,g14)
    c: Tangent(g13,g55) = 1.5708
    c: Tangent(g14,g55) = 1.5708
    c: PointOnObject(g58,g16)
    c: PointOnObject(g58,g17)
    c: Tangent(g16,g57) = -1.5708
    c: Tangent(g17,g57) = -1.5708
    c: PointOnObject(g60,g19)
    c: PointOnObject(g60,g20)
    c: Tangent(g19,g59) = 1.5708
    c: Tangent(g20,g59) = 1.5708
    c: PointOnObject(g62,g21)
    c: PointOnObject(g62,g22)
    c: Tangent(g21,g61) = 1.5708
    c: Tangent(g22,g61) = 1.5708
    c: PointOnObject(g64,g24)
    c: PointOnObject(g64,g25)
    c: Tangent(g24,g63) = -1.5708
    c: Tangent(g25,g63) = -1.5708
    c: PointOnObject(g66,g27)
    c: PointOnObject(g66,g28)
    c: Tangent(g27,g65) = -1.5708
    c: Tangent(g28,g65) = -1.5708
    c: PointOnObject(g68,g30)
    c: PointOnObject(g68,g31)
    c: Tangent(g30,g67) = 1.5708
    c: Tangent(g31,g67) = 1.5708
    c: PointOnObject(g70,g34)
    c: PointOnObject(g70,g35)
    c: Tangent(g34,g69) = -1.5708
    c: Tangent(g35,g69) = -1.5708
    c: PointOnObject(g72,g37)
    c: PointOnObject(g72,g38)
    c: Tangent(g37,g71) = 1.5708
    c: Tangent(g38,g71) = 1.5708
    c: PointOnObject(g74,g40)
    c: PointOnObject(g74,g41)
    c: Tangent(g40,g73) = 1.5708
    c: Tangent(g41,g73) = 1.5708
    c: PointOnObject(g76,g43)
    c: PointOnObject(g76,g44)
    c: Tangent(g43,g75) = -1.5708
    c: Tangent(g44,g75) = -1.5708
    c: Coincident(g10,g77)
    c: Coincident(g78,g8)
    c: PointOnObject(g80,g77)
    c: PointOnObject(g80,g78)
    c: Tangent(g77,g79) = 1.5708
    c: Tangent(g78,g79) = 1.5708
    c: Coincident(g78,g-8)
FEATURE [PartDesign::Body] Body
  Group = -> [ShapeBinder,Sketch]
  Origin = -> Origin001
FEATURE [App::Part] Part
  Group = -> [Body]
  Origin = -> Origin
